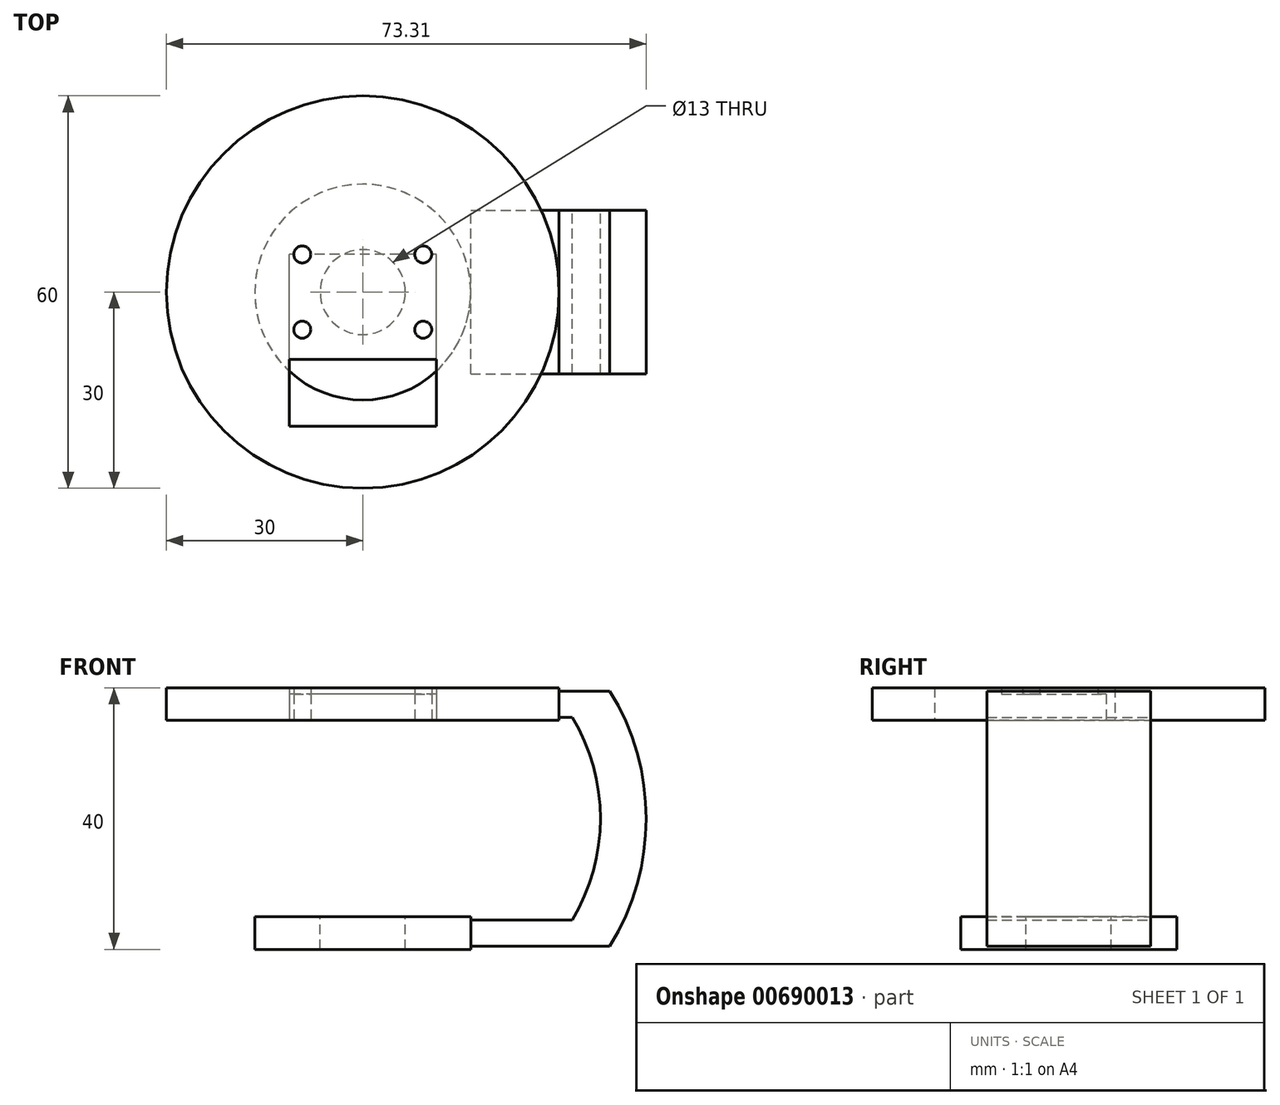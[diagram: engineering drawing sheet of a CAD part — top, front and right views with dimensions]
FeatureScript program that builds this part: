
annotation { "Feature Type Name" : "Feature", "Feature Type Description" : "" }
export const myFeature = defineFeature(function(context is Context, id is Id, definition is map)
    precondition{}
    {
        {
            var Q0;
            Q0=qCreatedBy(makeId("Front.planeOp"),FACE);
            var sketch = newSketch(context, id + "F0", { "sketchPlane" : qUnion([Q0])});
            skLineSegment(sketch, "E0.bottom", {"start": v(16.5, 2.5) * mm, "end": v(-16.5, 2.5) * mm});
            skLineSegment(sketch, "E0.top", {"start": v(16.5, -2.5) * mm, "end": v(-16.5, -2.5) * mm});
            skLineSegment(sketch, "E0.left", {"start": v(16.5, 2.5) * mm, "end": v(16.5, -2.5) * mm});
            skLineSegment(sketch, "E0.right", {"start": v(-16.5, 2.5) * mm, "end": v(-16.5, -2.5) * mm});
            skPoint(sketch, "E0.middle", {"position": v(0, 0) * mm});
            skLineSegment(sketch, "E1", {"start": v(0, 2.5) * mm, "end": v(0, -2.5) * mm});
            skLineSegment(sketch, "E2.bottom", {"start": v(0, -2) * mm, "end": v(32, -2) * mm});
            skLineSegment(sketch, "E2.top", {"start": v(0, 2) * mm, "end": v(32, 2) * mm});
            skLineSegment(sketch, "E2.left", {"start": v(0, -2) * mm, "end": v(0, 2) * mm});
            skLineSegment(sketch, "E2.right", {"start": v(32, -2) * mm, "end": v(32, 2) * mm});
            skLineSegment(sketch, "E3.bottom", {"start": v(30, 37.5) * mm, "end": v(-30, 37.5) * mm});
            skLineSegment(sketch, "E3.top", {"start": v(30, 32.5) * mm, "end": v(-30, 32.5) * mm});
            skLineSegment(sketch, "E3.left", {"start": v(30, 37.5) * mm, "end": v(30, 32.5) * mm});
            skLineSegment(sketch, "E3.right", {"start": v(-30, 37.5) * mm, "end": v(-30, 32.5) * mm});
            skPoint(sketch, "E3.middle", {"position": v(0, 35) * mm});
            skLineSegment(sketch, "E4", {"start": v(0, 37.5) * mm, "end": v(0, 32.5) * mm});
            skLineSegment(sketch, "E5.bottom", {"start": v(0, 33) * mm, "end": v(32, 33) * mm});
            skLineSegment(sketch, "E5.top", {"start": v(0, 37) * mm, "end": v(32, 37) * mm});
            skLineSegment(sketch, "E5.left", {"start": v(0, 33) * mm, "end": v(0, 37) * mm});
            skLineSegment(sketch, "E5.right", {"start": v(32, 33) * mm, "end": v(32, 37) * mm});
            skArc(sketch, "E6", {"start": v(32, 2) * mm, "mid": v(36.31, 17.5) * mm, "end": v(32, 33) * mm});
            skArc(sketch, "E7.0", {"start": v(37.76, -2) * mm, "mid": v(43.31, 17.5) * mm, "end": v(37.76, 37) * mm});
            skLineSegment(sketch, "E8", {"start": v(32, 37) * mm, "end": v(37.76, 37) * mm});
            skLineSegment(sketch, "E9", {"start": v(32, -2) * mm, "end": v(37.76, -2) * mm});
            skSolve(sketch);
        }
        {
            var Q0;
            {var subQ0=sQuery(id+"F0.wireOp",EDGE,"E0.right");Q0=makeQuery(id+"F0.imprint","IMPRINT",FACE,{"disambiguationData":[TD([[makeQuery(id+"F0.imprint","IMPRINT",EDGE,{"derivedFrom":subQ0}),1.0]])]});}
            var Q1;
            Q1=sQuery(id+"F0.wireOp",EDGE,"E1");
            revolve(context, id + "F1", {"entities" : qUnion([Q0]), "axis" : qUnion([Q1]), "revolveType" : RevolveType.FULL});
        }
        {
            var Q0;
            {var subQ0=sQuery(id+"F0.wireOp",EDGE,"E3.right");Q0=makeQuery(id+"F0.imprint","IMPRINT",FACE,{"disambiguationData":[TD([[makeQuery(id+"F0.imprint","IMPRINT",EDGE,{"derivedFrom":subQ0}),1.0]])]});}
            var Q1;
            Q1=sQuery(id+"F0.wireOp",EDGE,"E4");
            revolve(context, id + "F2", {"entities" : qUnion([Q0]), "axis" : qUnion([Q1]), "revolveType" : RevolveType.FULL});
        }
        {
            var Q0;
            {var subQ5=sQuery(id+"F0.wireOp",EDGE,"E2.right");Q0=makeQuery(id+"F0.imprint","IMPRINT",FACE,{"disambiguationData":[TD([[makeQuery(id+"F0.imprint","IMPRINT",EDGE,{"derivedFrom":subQ5}),1.0]])]});}
            var Q1;
            Q1=makeQuery(id+"F0.imprint","IMPRINT",FACE,{"disambiguationData":[TD([[makeQuery(id+"F0.imprint","IMPRINT",EDGE,{"derivedFrom":sQuery(id+"F0.wireOp",EDGE,"E2.right")}),-1.0]])]});
            var Q2;
            {var subQ5=sQuery(id+"F0.wireOp",EDGE,"E5.right");Q2=makeQuery(id+"F0.imprint","IMPRINT",FACE,{"disambiguationData":[TD([[makeQuery(id+"F0.imprint","IMPRINT",EDGE,{"derivedFrom":subQ5}),1.0]])]});}
            var Q3;
            {var subQ5=sQuery(id+"F0.wireOp",EDGE,"E2.left");Q3=makeQuery(id+"F0.imprint","IMPRINT",FACE,{"disambiguationData":[TD([[makeQuery(id+"F0.imprint","IMPRINT",EDGE,{"derivedFrom":subQ5}),-1.0]])]});}
            var Q4;
            {var subQ5=sQuery(id+"F0.wireOp",EDGE,"E5.left");Q4=makeQuery(id+"F0.imprint","IMPRINT",FACE,{"disambiguationData":[TD([[makeQuery(id+"F0.imprint","IMPRINT",EDGE,{"derivedFrom":subQ5}),-1.0]])]});}
            extrude(context, id + "F3", {"entities" : qUnion([Q0, Q1, Q2, Q3, Q4]), "endBound" : BoundingType.SYMMETRIC, "depth" : 25 * mm, "offsetDistance" : 25 * mm});
        }
        {
            var Q0;
            Q0=makeQuery(id+"F1.opRevolve","SWEPT_FACE",FACE,{"disambiguationData":[OSD([sQuery(id+"F0.wireOp",EDGE,"E0.bottom")])]});
            var sketch = newSketch(context, id + "F4", { "sketchPlane" : qUnion([Q0])});
            skCircle(sketch, "E10", {"center": v(0, 0) * mm, "radius": 12 * mm});
            skPoint(sketch, "E11", {"position": v(0, 12) * mm});
            skSolve(sketch);
        }
        {
            var Q0;
            Q0=sQuery(id+"F4.wireOp",VERTEX,"E11");
            var Q1;
            Q1=makeQuery(id+"F2.opRevolve","SWEPT_BODY",BODY,{"disambiguationData":[OSD([sQuery(id+"F0.wireOp",EDGE,"E3.bottom"),sQuery(id+"F0.wireOp",EDGE,"E3.top"),sQuery(id+"F0.wireOp",EDGE,"E3.right"),sQuery(id+"F0.wireOp",EDGE,"E4"),sQuery(id+"F0.wireOp",EDGE,"E5.left")])]});
            hole(context, id + "F5", {"style" : HoleStyle.SIMPLE, "endStyle" : HoleEndStyle.THROUGH, "holeDiameter" : 4 * mm, "isTappedThrough" : true, "tappedDepth" : 12.7 * mm, "tapClearance" : 3, "locations" : qUnion([Q0]), "scope" : qUnion([Q1]), "majorDiameter" : 5 * mm});
        }
        {
            var Q0;
            Q0=makeQuery(id+"F1.opRevolve","SWEPT_FACE",FACE,{"disambiguationData":[OSD([sQuery(id+"F0.wireOp",EDGE,"E0.bottom")])]});
            var sketch = newSketch(context, id + "F6", { "sketchPlane" : qUnion([Q0])});
            skCircle(sketch, "E12", {"center": v(0, 0) * mm, "radius": 6.5 * mm});
            skSolve(sketch);
        }
        {
            var Q0;
            Q0=makeQuery(id+"F6.imprint","IMPRINT",FACE,{"disambiguationData":[TD([[makeQuery(id+"F6.imprint","IMPRINT",EDGE,{"derivedFrom":sQuery(id+"F6.wireOp",EDGE,"E12")}),1.0]])]});
            extrude(context, id + "F7", {"entities" : qUnion([Q0]), "operationType" : NewBodyOperationType.REMOVE, "oppositeDirection" : true, "depth" : 6 * mm, "offsetDistance" : 25 * mm});
        }
        {
            var Q0;
            Q0=makeQuery(id+"F2.opRevolve","SWEPT_FACE",FACE,{"disambiguationData":[OSD([sQuery(id+"F0.wireOp",EDGE,"E3.top")])]});
            var sketch = newSketch(context, id + "F8", { "sketchPlane" : qUnion([Q0])});
            skLineSegment(sketch, "E13.bottom", {"start": v(11.25, 5.75) * mm, "end": v(-11.25, 5.75) * mm});
            skLineSegment(sketch, "E13.top", {"start": v(11.25, -5.75) * mm, "end": v(-11.25, -5.75) * mm});
            skLineSegment(sketch, "E13.left", {"start": v(11.25, 5.75) * mm, "end": v(11.25, -5.75) * mm});
            skLineSegment(sketch, "E13.right", {"start": v(-11.25, 5.75) * mm, "end": v(-11.25, -5.75) * mm});
            skPoint(sketch, "E13.middle", {"position": v(0, 0) * mm});
            skLineSegment(sketch, "E14.bottom", {"start": v(-11.25, -5.75) * mm, "end": v(10.8, -5.75) * mm});
            skLineSegment(sketch, "E14.top", {"start": v(-11.25, 20.5) * mm, "end": v(11.25, 20.5) * mm});
            skLineSegment(sketch, "E14.left", {"start": v(-11.25, -8) * mm, "end": v(-11.25, 20.5) * mm});
            skLineSegment(sketch, "E14.right", {"start": v(11.25, -8) * mm, "end": v(11.25, 20.5) * mm});
            skLineSegment(sketch, "E15", {"start": v(-11.25, -8) * mm, "end": v(11.25, -8) * mm});
            skPoint(sketch, "E16", {"position": v(-9.25, -5.75) * mm});
            skPoint(sketch, "E17", {"position": v(9.25, -5.75) * mm});
            skPoint(sketch, "E18", {"position": v(9.25, 5.75) * mm});
            skPoint(sketch, "E19", {"position": v(-9.25, 5.75) * mm});
            skSolve(sketch);
        }
        {
            var Q0;
            Q0=sQuery(id+"F8.wireOp",VERTEX,"E16");
            var Q1;
            Q1=sQuery(id+"F8.wireOp",VERTEX,"E19");
            var Q2;
            Q2=sQuery(id+"F8.wireOp",VERTEX,"E18");
            var Q3;
            Q3=sQuery(id+"F8.wireOp",VERTEX,"E17");
            var Q4;
            Q4=makeQuery(id+"F2.opRevolve","SWEPT_BODY",BODY,{"disambiguationData":[OSD([sQuery(id+"F0.wireOp",EDGE,"E3.bottom"),sQuery(id+"F0.wireOp",EDGE,"E3.top"),sQuery(id+"F0.wireOp",EDGE,"E3.right"),sQuery(id+"F0.wireOp",EDGE,"E4"),sQuery(id+"F0.wireOp",EDGE,"E5.left")])]});
            hole(context, id + "F9", {"style" : HoleStyle.SIMPLE, "endStyle" : HoleEndStyle.THROUGH, "holeDiameter" : 2.6 * mm, "isTappedThrough" : true, "tappedDepth" : 12.7 * mm, "tapClearance" : 3, "locations" : qUnion([Q0, Q1, Q2, Q3]), "scope" : qUnion([Q4])});
        }
        {
            var Q0;
            {var subQ0=sQuery(id+"F8.wireOp",EDGE,"E14.bottom");Q0=makeQuery(id+"F8.imprint","IMPRINT",FACE,{"disambiguationData":[TD([[makeQuery(id+"F8.imprint","IMPRINT",EDGE,{"derivedFrom":subQ0}),-1.0]])]});}
            var Q1;
            {var subQ0=sQuery(id+"F8.wireOp",EDGE,"E13.bottom");Q1=makeQuery(id+"F8.imprint","IMPRINT",FACE,{"disambiguationData":[TD([[makeQuery(id+"F8.imprint","IMPRINT",EDGE,{"derivedFrom":subQ0}),1.0]])]});}
            var Q2;
            {var subQ0=sQuery(id+"F8.wireOp",EDGE,"E13.bottom");Q2=makeQuery(id+"F8.imprint","IMPRINT",FACE,{"disambiguationData":[TD([[makeQuery(id+"F8.imprint","IMPRINT",EDGE,{"derivedFrom":subQ0}),-1.0]])]});}
            extrude(context, id + "F10", {"entities" : qUnion([Q0, Q1, Q2]), "operationType" : NewBodyOperationType.REMOVE, "oppositeDirection" : true, "depth" : 4 * mm, "offsetDistance" : 25 * mm});
        }
        {
            var Q0;
            Q0=makeQuery(id+"F10.boolean.opBoolean","COPY",FACE,{"derivedFrom":makeQuery(id+"F10.opExtrude","CAP_FACE",FACE,{"disambiguationData":[OSD([sQuery(id+"F8.wireOp",EDGE,"E14.top"),sQuery(id+"F8.wireOp",EDGE,"E14.left"),sQuery(id+"F8.wireOp",EDGE,"E14.right"),sQuery(id+"F8.wireOp",EDGE,"E15")])],"isStart":false})});
            var sketch = newSketch(context, id + "F11", { "sketchPlane" : qUnion([Q0])});
            skLineSegment(sketch, "E20.bottom", {"start": v(11.25, 20.5) * mm, "end": v(-11.25, 20.5) * mm});
            skLineSegment(sketch, "E20.top", {"start": v(11.25, 10.27) * mm, "end": v(-11.25, 10.27) * mm});
            skLineSegment(sketch, "E20.left", {"start": v(11.25, 20.5) * mm, "end": v(11.25, 10.27) * mm});
            skLineSegment(sketch, "E20.right", {"start": v(-11.25, 20.5) * mm, "end": v(-11.25, 10.27) * mm});
            skSolve(sketch);
        }
        {
            var Q0;
            Q0=makeQuery(id+"F11.imprint","IMPRINT",FACE,{"disambiguationData":[TD([[makeQuery(id+"F11.imprint","IMPRINT",EDGE,{"derivedFrom":sQuery(id+"F11.wireOp",EDGE,"E20.bottom")}),-1.0]])]});
            extrude(context, id + "F12", {"entities" : qUnion([Q0]), "operationType" : NewBodyOperationType.REMOVE, "oppositeDirection" : true, "depth" : 25 * mm, "offsetDistance" : 25 * mm});
        }
    });
